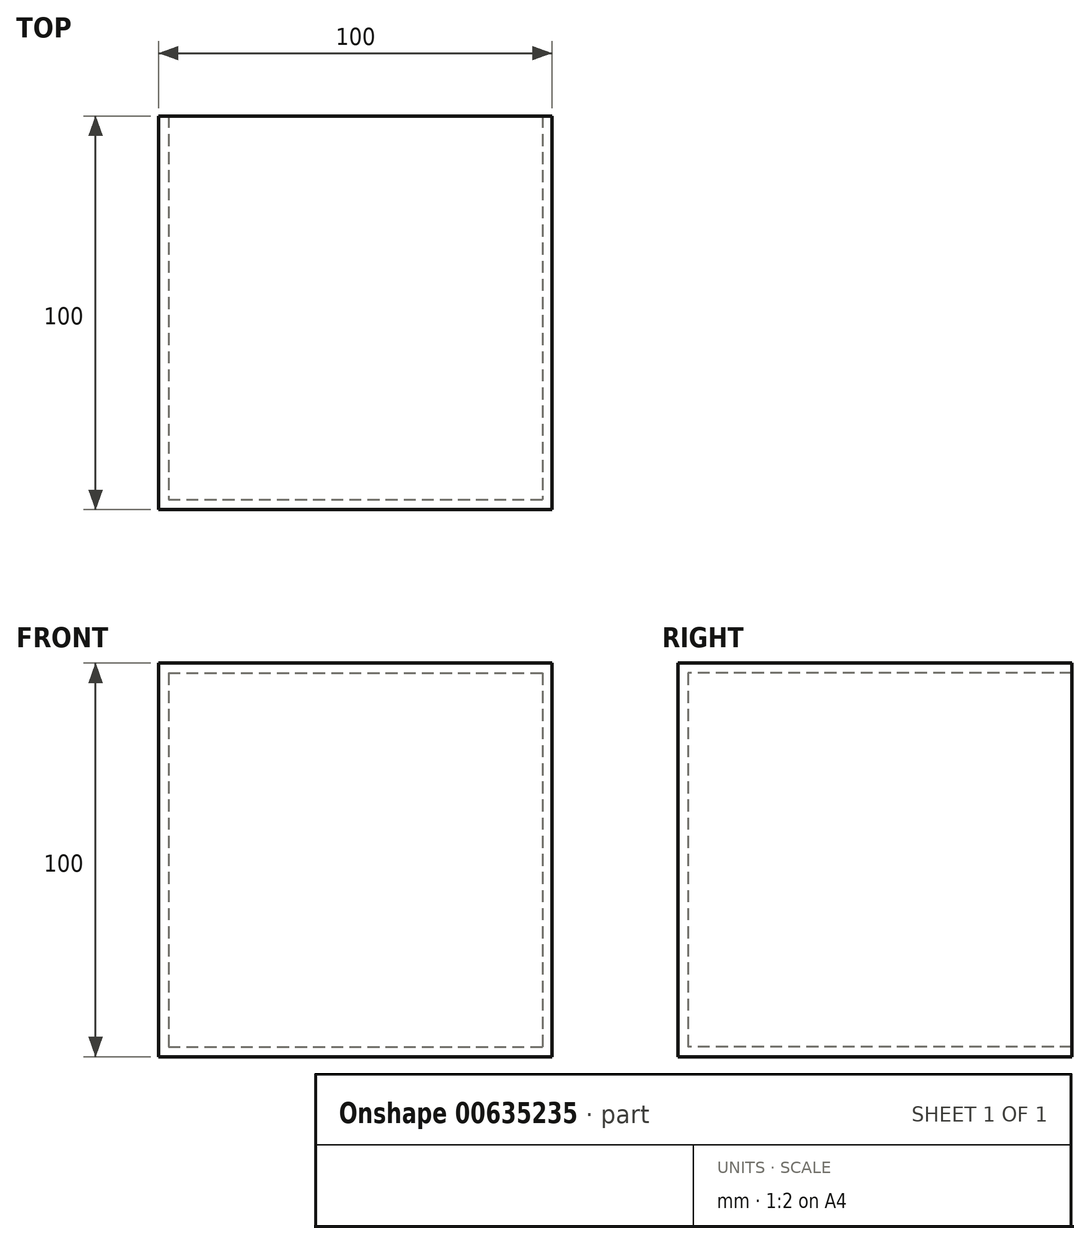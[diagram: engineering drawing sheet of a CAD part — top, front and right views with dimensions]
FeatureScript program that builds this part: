
annotation { "Feature Type Name" : "Feature", "Feature Type Description" : "" }
export const myFeature = defineFeature(function(context is Context, id is Id, definition is map)
    precondition{}
    {
        {
            var Q0;
            Q0=qCreatedBy(makeId("Top.planeOp"),FACE);
            var sketch = newSketch(context, id + "F0", { "sketchPlane" : qUnion([Q0])});
            skLineSegment(sketch, "E0.bottom", {"start": v(-50, 50) * mm, "end": v(50, 50) * mm});
            skLineSegment(sketch, "E0.top", {"start": v(-50, -50) * mm, "end": v(50, -50) * mm});
            skLineSegment(sketch, "E0.left", {"start": v(-50, 50) * mm, "end": v(-50, -50) * mm});
            skLineSegment(sketch, "E0.right", {"start": v(50, 50) * mm, "end": v(50, -50) * mm});
            skLineSegment(sketch, "E1", {"start": v(-30, 50) * mm, "end": v(-30, -50) * mm, "construction": true});
            skLineSegment(sketch, "E2", {"start": v(-20, 50) * mm, "end": v(-20, -50) * mm, "construction": true});
            skLineSegment(sketch, "E3", {"start": v(-10, 50) * mm, "end": v(-10, -50) * mm, "construction": true});
            skLineSegment(sketch, "E4", {"start": v(10, 50) * mm, "end": v(10, -50) * mm, "construction": true});
            skLineSegment(sketch, "E5", {"start": v(0, 50) * mm, "end": v(0, -50) * mm, "construction": true});
            skLineSegment(sketch, "E6", {"start": v(20, 50) * mm, "end": v(20, -50) * mm, "construction": true});
            skLineSegment(sketch, "E7", {"start": v(30, 50) * mm, "end": v(30, -50) * mm, "construction": true});
            skLineSegment(sketch, "E8", {"start": v(40, 50) * mm, "end": v(40, -50) * mm, "construction": true});
            skLineSegment(sketch, "E9", {"start": v(-40, 50) * mm, "end": v(-40, -50) * mm, "construction": true});
            skLineSegment(sketch, "E10", {"start": v(-50, 40) * mm, "end": v(50, 40) * mm, "construction": true});
            skLineSegment(sketch, "E11", {"start": v(-50, 30) * mm, "end": v(50, 30) * mm, "construction": true});
            skLineSegment(sketch, "E12", {"start": v(-50, 20) * mm, "end": v(50, 20) * mm, "construction": true});
            skLineSegment(sketch, "E13", {"start": v(-50, 10) * mm, "end": v(50, 10) * mm, "construction": true});
            skLineSegment(sketch, "E14", {"start": v(-50, -40) * mm, "end": v(50, -40) * mm, "construction": true});
            skLineSegment(sketch, "E15", {"start": v(50, -30) * mm, "end": v(-50, -30) * mm, "construction": true});
            skLineSegment(sketch, "E16", {"start": v(-50, -20) * mm, "end": v(50, -20) * mm, "construction": true});
            skLineSegment(sketch, "E17", {"start": v(-50, -10) * mm, "end": v(50, -10) * mm, "construction": true});
            skLineSegment(sketch, "E18", {"start": v(-50, 0) * mm, "end": v(50, 0) * mm, "construction": true});
            skSolve(sketch);
        }
        {
            var Q0;
            Q0=makeQuery(id+"F0.imprint","IMPRINT",FACE,{"disambiguationData":[TD([[makeQuery(id+"F0.imprint","IMPRINT",EDGE,{"derivedFrom":sQuery(id+"F0.wireOp",EDGE,"E0.bottom")}),-1.0]])]});
            extrude(context, id + "F1", {"entities" : qUnion([Q0]), "depth" : 100 * mm, "offsetDistance" : 25 * mm});
        }
        {
            var Q0;
            Q0=makeQuery(id+"F1.opExtrude","SWEPT_FACE",FACE,{"disambiguationData":[OSD([sQuery(id+"F0.wireOp",EDGE,"E0.bottom")])]});
            shell(context, id + "F2", {"entities" : qUnion([Q0]), "thickness" : 2.5 * mm});
        }
    });
